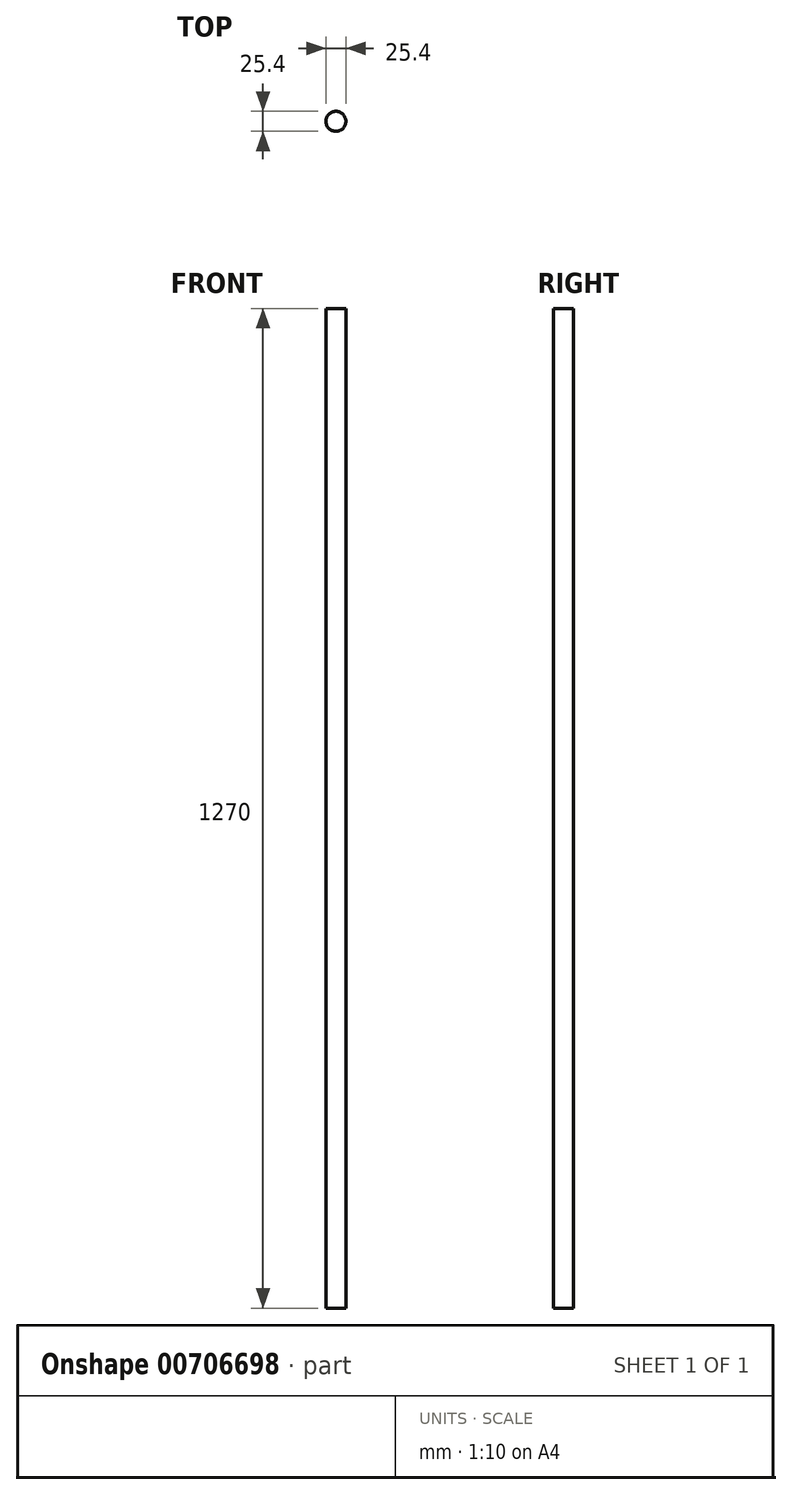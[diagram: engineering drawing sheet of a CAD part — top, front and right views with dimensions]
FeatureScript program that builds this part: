
annotation { "Feature Type Name" : "Feature", "Feature Type Description" : "" }
export const myFeature = defineFeature(function(context is Context, id is Id, definition is map)
    precondition{}
    {
        {
            var Q0;
            Q0=qCreatedBy(makeId("Top.planeOp"),FACE);
            var sketch = newSketch(context, id + "F0", { "sketchPlane" : qUnion([Q0])});
            skCircle(sketch, "E0", {"center": v(0, 0) * mm, "radius": 12.7 * mm});
            skSolve(sketch);
        }
        {
            var Q0;
            Q0=makeQuery(id+"F0.imprint","IMPRINT",FACE,{"disambiguationData":[TD([[makeQuery(id+"F0.imprint","IMPRINT",EDGE,{"derivedFrom":sQuery(id+"F0.wireOp",EDGE,"E0")}),1.0]])]});
            extrude(context, id + "F1", {"entities" : qUnion([Q0]), "depth" : 1270 * mm, "offsetDistance" : 25.4 * mm});
        }
    });
